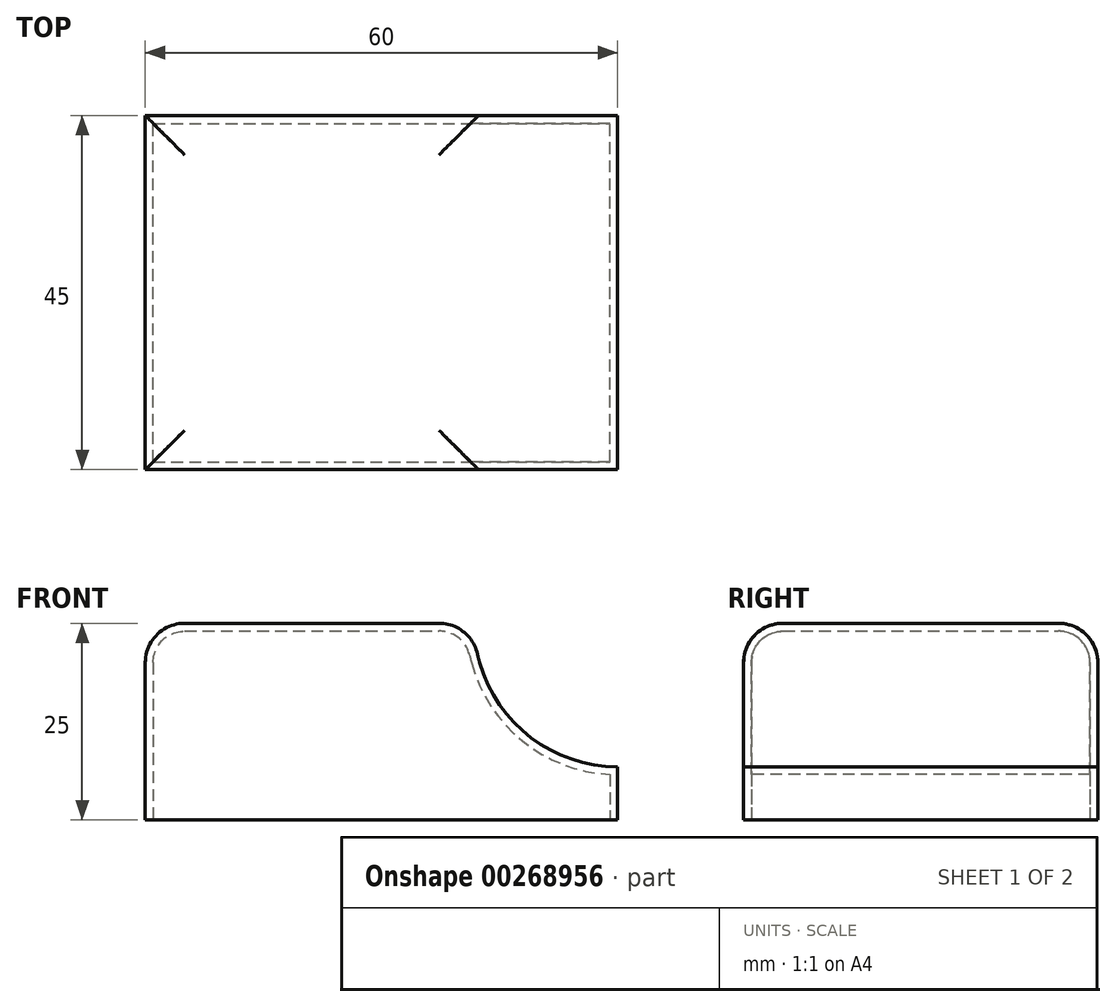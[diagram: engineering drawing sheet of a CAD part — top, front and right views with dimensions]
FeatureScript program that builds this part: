
annotation { "Feature Type Name" : "Feature", "Feature Type Description" : "" }
export const myFeature = defineFeature(function(context is Context, id is Id, definition is map)
    precondition{}
    {
        {
            var Q0;
            Q0=qCreatedBy(makeId("Top.planeOp"),FACE);
            var sketch = newSketch(context, id + "F0", { "sketchPlane" : qUnion([Q0])});
            skLineSegment(sketch, "E0.bottom", {"start": v(1.26, 0) * mm, "end": v(61.26, 0) * mm});
            skLineSegment(sketch, "E0.top", {"start": v(1.26, 45) * mm, "end": v(61.26, 45) * mm});
            skLineSegment(sketch, "E0.left", {"start": v(1.26, 0) * mm, "end": v(1.26, 45) * mm});
            skLineSegment(sketch, "E0.right", {"start": v(61.26, 0) * mm, "end": v(61.26, 45) * mm});
            skSolve(sketch);
        }
        {
            var Q0;
            Q0 = qSketchRegion(id + "F0", true);
            extrude(context, id + "F1", {"entities" : qUnion([Q0]), "depth" : 25 * mm});
        }
        {
            var Q0;
            Q0=makeQuery(id+"F1.opExtrude","SWEPT_FACE",FACE,{"disambiguationData":[OSD([sQuery(id+"F0.wireOp",EDGE,"E0.bottom")])]});
            var sketch = newSketch(context, id + "F2", { "sketchPlane" : qUnion([Q0])});
            skCircle(sketch, "E1", {"center": v(61.26, 25) * mm, "radius": 18.23 * mm});
            skSolve(sketch);
        }
        {
            var Q0;
            Q0 = qSketchRegion(id + "F2", true);
            extrude(context, id + "F3", {"entities" : qUnion([Q0]), "operationType" : NewBodyOperationType.REMOVE, "endBound" : BoundingType.THROUGH_ALL, "oppositeDirection" : true, "depth" : 25 * mm});
        }
        {
            var Q0;
            Q0=makeQuery(id+"F1.opExtrude","CAP_FACE",FACE,{"disambiguationData":[OSD([sQuery(id+"F0.wireOp",EDGE,"E0.bottom"),sQuery(id+"F0.wireOp",EDGE,"E0.top"),sQuery(id+"F0.wireOp",EDGE,"E0.left"),sQuery(id+"F0.wireOp",EDGE,"E0.right")])],"isStart":false});
            fillet(context, id + "F4", {"entities" : qUnion([Q0]), "radius" : 5 * mm, "tangentPropagation" : true, "allowEdgeOverflow" : false});
        }
        {
            var Q0;
            Q0=makeQuery(id+"F1.opExtrude","CAP_FACE",FACE,{"disambiguationData":[OSD([sQuery(id+"F0.wireOp",EDGE,"E0.bottom"),sQuery(id+"F0.wireOp",EDGE,"E0.top"),sQuery(id+"F0.wireOp",EDGE,"E0.left"),sQuery(id+"F0.wireOp",EDGE,"E0.right")])],"isStart":true});
            shell(context, id + "F5", {"entities" : qUnion([Q0]), "thickness" : 1 * mm});
        }
    });
